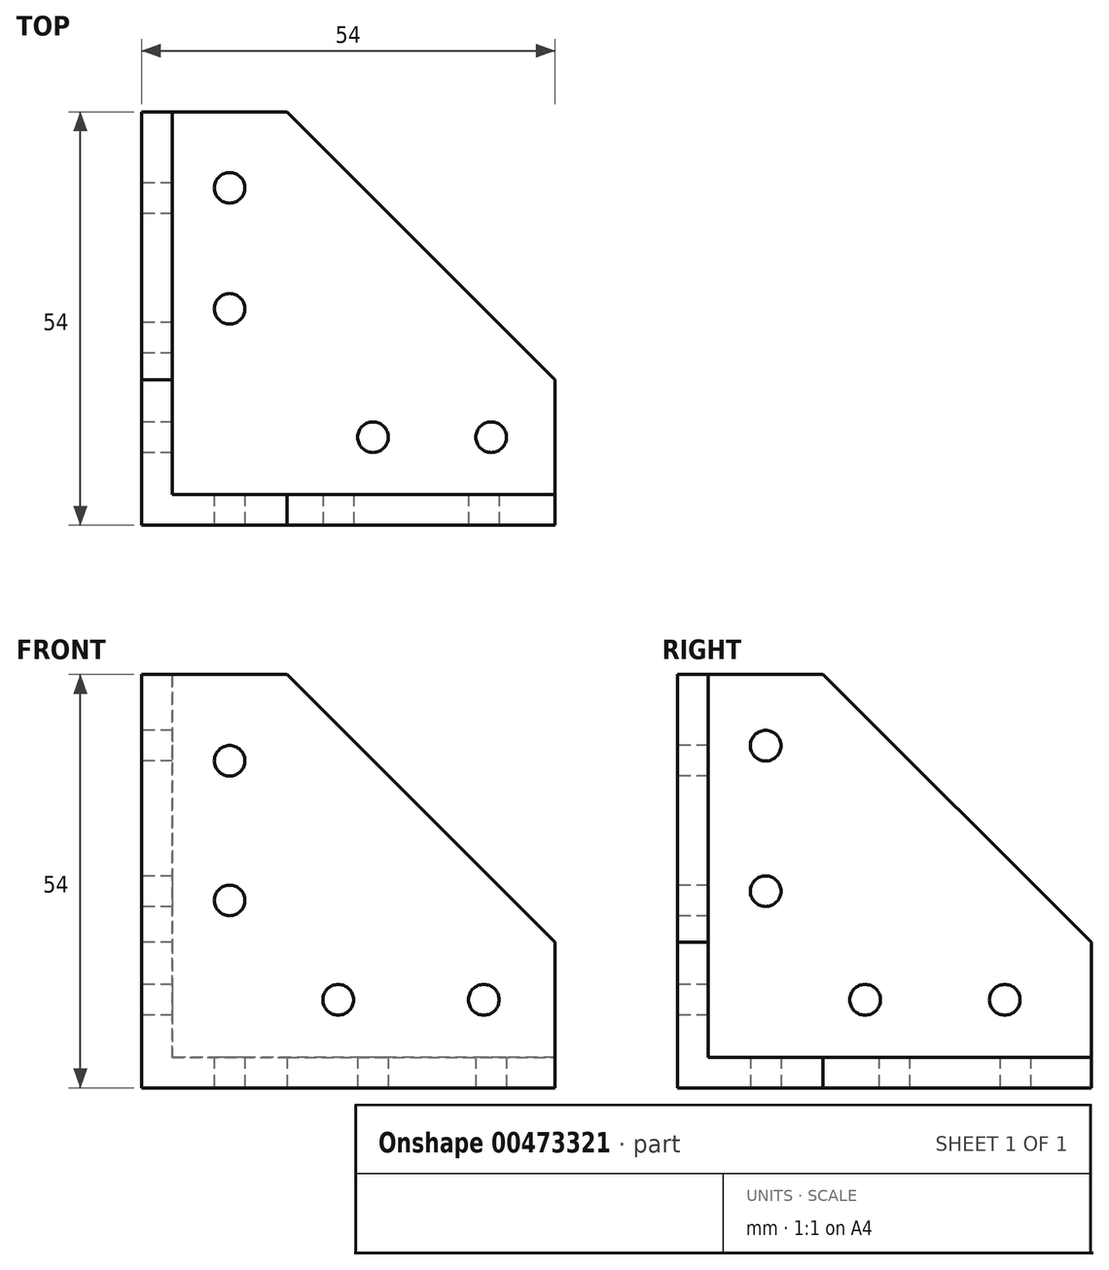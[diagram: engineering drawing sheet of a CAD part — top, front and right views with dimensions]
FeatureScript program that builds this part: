
annotation { "Feature Type Name" : "Feature", "Feature Type Description" : "" }
export const myFeature = defineFeature(function(context is Context, id is Id, definition is map)
    precondition{}
    {
        {
            var Q0;
            Q0=qCreatedBy(makeId("Top.planeOp"),FACE);
            var sketch = newSketch(context, id + "F0", { "sketchPlane" : qUnion([Q0])});
            skLineSegment(sketch, "E0.top", {"start": v(0, 50) * mm, "end": v(15, 50) * mm});
            skLineSegment(sketch, "E0.right", {"start": v(50, 0) * mm, "end": v(50, 15) * mm});
            skLineSegment(sketch, "E1.top", {"start": v(0, 15) * mm, "end": v(15, 15) * mm, "construction": true});
            skLineSegment(sketch, "E1.right", {"start": v(15, 0) * mm, "end": v(15, 15) * mm, "construction": true});
            skLineSegment(sketch, "E2", {"start": v(15, 15) * mm, "end": v(15, 50) * mm, "construction": true});
            skLineSegment(sketch, "E3", {"start": v(15, 15) * mm, "end": v(50, 15) * mm, "construction": true});
            skLineSegment(sketch, "E4", {"start": v(15, 50) * mm, "end": v(50, 15) * mm});
            skLineSegment(sketch, "E5.bottom", {"start": v(0, 50) * mm, "end": v(-4, 50) * mm});
            skLineSegment(sketch, "E5.right", {"start": v(-4, 50) * mm, "end": v(-4, 0) * mm});
            skLineSegment(sketch, "E6", {"start": v(50, 0) * mm, "end": v(50, -4) * mm});
            skLineSegment(sketch, "E7", {"start": v(50, -4) * mm, "end": v(-4, -4) * mm});
            skLineSegment(sketch, "E8", {"start": v(-4, -4) * mm, "end": v(-4, 0) * mm});
            skPoint(sketch, "E9", {"position": v(7.5, 50) * mm});
            skPoint(sketch, "E10", {"position": v(50, 7.5) * mm});
            skCircle(sketch, "E11", {"center": v(7.5, 40.07) * mm, "radius": 2 * mm});
            skCircle(sketch, "E12", {"center": v(7.5, 24.27) * mm, "radius": 2 * mm});
            skCircle(sketch, "E13", {"center": v(26.22, 7.5) * mm, "radius": 2 * mm});
            skPoint(sketch, "E13.centerSnap0", {"position": v(15, 7.5) * mm});
            skCircle(sketch, "E14", {"center": v(41.65, 7.5) * mm, "radius": 2 * mm});
            skSolve(sketch);
        }
        {
            var Q0;
            Q0 = qSketchRegion(id + "F0", true);
            extrude(context, id + "F1", {"entities" : qUnion([Q0]), "depth" : 4 * mm});
        }
        {
            var Q0;
            Q0=makeQuery(id+"F1.opExtrude","SWEPT_FACE",FACE,{"disambiguationData":[OSD([sQuery(id+"F0.wireOp",EDGE,"E7")])]});
            var sketch = newSketch(context, id + "F2", { "sketchPlane" : qUnion([Q0])});
            skLineSegment(sketch, "E15", {"start": v(-4, 4) * mm, "end": v(-4, 54) * mm});
            skLineSegment(sketch, "E16", {"start": v(-4, 54) * mm, "end": v(15, 54) * mm});
            skLineSegment(sketch, "E17", {"start": v(50, 4) * mm, "end": v(50, 19) * mm});
            skLineSegment(sketch, "E18", {"start": v(50, 19) * mm, "end": v(15, 54) * mm});
            skPoint(sketch, "E19", {"position": v(7.5, 54) * mm});
            skPoint(sketch, "E20", {"position": v(50, 11.5) * mm});
            skCircle(sketch, "E21", {"center": v(7.5, 42.72) * mm, "radius": 2 * mm});
            skCircle(sketch, "E22", {"center": v(7.5, 24.48) * mm, "radius": 2 * mm});
            skCircle(sketch, "E23", {"center": v(40.7, 11.5) * mm, "radius": 2 * mm});
            skCircle(sketch, "E24", {"center": v(21.68, 11.5) * mm, "radius": 2 * mm});
            skLineSegment(sketch, "E25", {"start": v(-4, 4) * mm, "end": v(50, 4) * mm});
            skSolve(sketch);
        }
        {
            var Q0;
            Q0 = qSketchRegion(id + "F2", true);
            extrude(context, id + "F3", {"entities" : qUnion([Q0]), "operationType" : NewBodyOperationType.ADD, "oppositeDirection" : true, "depth" : 4 * mm});
        }
        {
            var Q0;
            Q0=makeQuery(id+"F3.boolean.opBoolean","MERGE",FACE,{"derivedFrom":[makeQuery(id+"F1.opExtrude","SWEPT_FACE",FACE,{"disambiguationData":[OSD([sQuery(id+"F0.wireOp",EDGE,"E5.right"),sQuery(id+"F0.wireOp",EDGE,"E8")])]}),makeQuery(id+"F3.opExtrude","SWEPT_FACE",FACE,{"disambiguationData":[OSD([sQuery(id+"F2.wireOp",EDGE,"E15")])]})]});
            var sketch = newSketch(context, id + "F4", { "sketchPlane" : qUnion([Q0])});
            skLineSegment(sketch, "E26", {"start": v(0, 0) * mm, "end": v(-50, 0) * mm});
            skLineSegment(sketch, "E27", {"start": v(-50, 0) * mm, "end": v(-50, 19) * mm});
            skLineSegment(sketch, "E28", {"start": v(0, 54) * mm, "end": v(-15, 54) * mm});
            skLineSegment(sketch, "E29", {"start": v(-15, 54) * mm, "end": v(-50, 19) * mm});
            skPoint(sketch, "E30", {"position": v(-50, 11.5) * mm});
            skPoint(sketch, "E31", {"position": v(-7.5, 54) * mm});
            skCircle(sketch, "E32", {"center": v(-38.72, 11.5) * mm, "radius": 2 * mm});
            skCircle(sketch, "E33", {"center": v(-20.48, 11.5) * mm, "radius": 2 * mm});
            skCircle(sketch, "E34", {"center": v(-7.5, 44.7) * mm, "radius": 2 * mm});
            skCircle(sketch, "E35", {"center": v(-7.5, 25.68) * mm, "radius": 2 * mm});
            skLineSegment(sketch, "E36", {"start": v(0, 0) * mm, "end": v(0, 54) * mm});
            skSolve(sketch);
        }
        {
            var Q0;
            Q0 = qSketchRegion(id + "F4", true);
            extrude(context, id + "F5", {"entities" : qUnion([Q0]), "operationType" : NewBodyOperationType.ADD, "oppositeDirection" : true, "depth" : 4 * mm});
        }
    });
